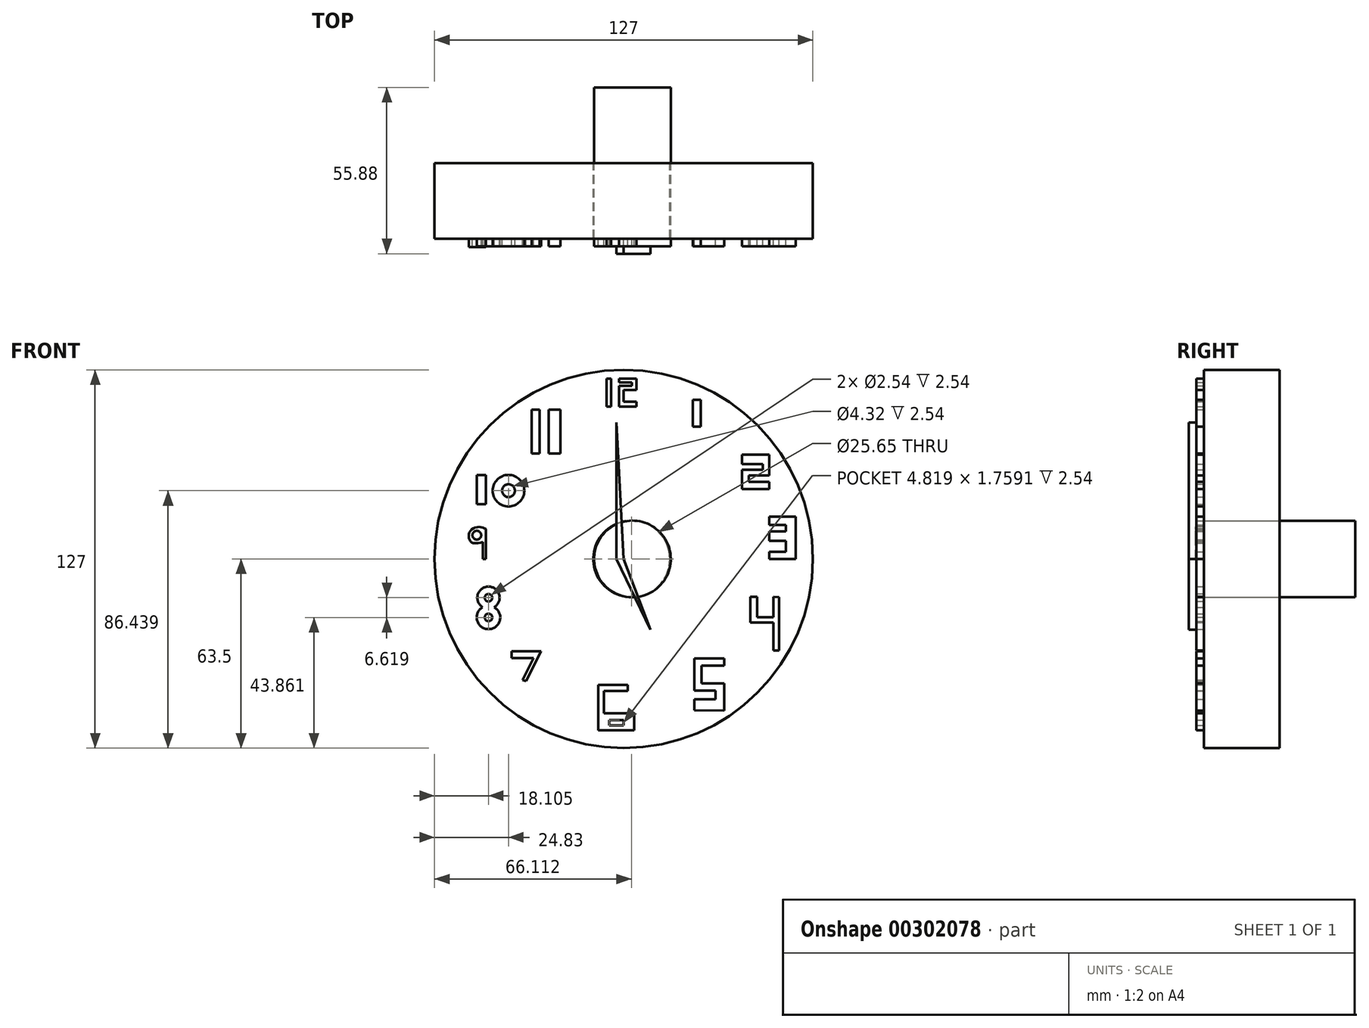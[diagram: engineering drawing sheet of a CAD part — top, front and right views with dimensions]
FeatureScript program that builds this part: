
annotation { "Feature Type Name" : "Feature", "Feature Type Description" : "" }
export const myFeature = defineFeature(function(context is Context, id is Id, definition is map)
    precondition{}
    {
        {
            var Q0;
            Q0=qCreatedBy(makeId("Front.planeOp"),FACE);
            var sketch = newSketch(context, id + "F0", { "sketchPlane" : qUnion([Q0])});
            skCircle(sketch, "E0", {"center": v(0, 0) * mm, "radius": 63.5 * mm});
            skSolve(sketch);
        }
        {
            var Q0;
            Q0 = qSketchRegion(id + "F0", true);
            extrude(context, id + "F1", {"entities" : qUnion([Q0]), "depth" : 25.4 * mm});
        }
        {
            var Q0;
            Q0=makeQuery(id+"F1.opExtrude","CAP_FACE",FACE,{"disambiguationData":[OSD([sQuery(id+"F0.wireOp",EDGE,"E0")])],"isStart":false});
            var sketch = newSketch(context, id + "F2", { "sketchPlane" : qUnion([Q0])});
            skLineSegment(sketch, "E1", {"start": v(-5.79, 60.54) * mm, "end": v(-4.25, 60.54) * mm});
            skLineSegment(sketch, "E2", {"start": v(0, 60.54) * mm, "end": v(4.26, 60.54) * mm});
            skLineSegment(sketch, "E3", {"start": v(4.26, 60.54) * mm, "end": v(4.26, 56.77) * mm});
            skLineSegment(sketch, "E4", {"start": v(4.26, 56.77) * mm, "end": v(0, 56.77) * mm});
            skLineSegment(sketch, "E5", {"start": v(0, 56.77) * mm, "end": v(0, 52.86) * mm});
            skLineSegment(sketch, "E6", {"start": v(0, 52.86) * mm, "end": v(4.26, 52.86) * mm});
            skLineSegment(sketch, "E7", {"start": v(4.26, 52.86) * mm, "end": v(4.26, 51.19) * mm});
            skLineSegment(sketch, "E8", {"start": v(4.26, 51.19) * mm, "end": v(0, 51.19) * mm});
            skLineSegment(sketch, "E9", {"start": v(0, 51.19) * mm, "end": v(-1.6, 51.19) * mm});
            skLineSegment(sketch, "E10", {"start": v(-1.6, 51.19) * mm, "end": v(-1.6, 58.17) * mm});
            skLineSegment(sketch, "E11", {"start": v(-1.6, 58.17) * mm, "end": v(2.73, 58.17) * mm});
            skLineSegment(sketch, "E12", {"start": v(2.73, 58.17) * mm, "end": v(2.73, 59.28) * mm});
            skLineSegment(sketch, "E13", {"start": v(2.73, 59.28) * mm, "end": v(-1.6, 59.28) * mm});
            skLineSegment(sketch, "E14", {"start": v(-1.6, 59.28) * mm, "end": v(-1.6, 60.54) * mm});
            skLineSegment(sketch, "E15", {"start": v(-1.6, 60.54) * mm, "end": v(0, 60.54) * mm});
            skLineSegment(sketch, "E16", {"start": v(-5.79, 60.54) * mm, "end": v(-5.79, 51.19) * mm});
            skLineSegment(sketch, "E17", {"start": v(-5.79, 51.19) * mm, "end": v(-4.25, 51.19) * mm});
            skLineSegment(sketch, "E18", {"start": v(-4.25, 51.19) * mm, "end": v(-4.25, 60.54) * mm});
            skLineSegment(sketch, "E19", {"start": v(23.23, 53.4) * mm, "end": v(23.23, 44.44) * mm});
            skLineSegment(sketch, "E20", {"start": v(23.23, 44.44) * mm, "end": v(25.84, 44.44) * mm});
            skLineSegment(sketch, "E21", {"start": v(25.84, 44.44) * mm, "end": v(25.84, 53.52) * mm});
            skLineSegment(sketch, "E22", {"start": v(25.84, 53.52) * mm, "end": v(23.23, 53.4) * mm});
            skLineSegment(sketch, "E23", {"start": v(39.65, 34.98) * mm, "end": v(48.85, 34.98) * mm});
            skLineSegment(sketch, "E24", {"start": v(39.65, 34.98) * mm, "end": v(39.65, 31.87) * mm});
            skLineSegment(sketch, "E25", {"start": v(39.65, 31.87) * mm, "end": v(46.74, 31.87) * mm});
            skLineSegment(sketch, "E26", {"start": v(46.74, 31.87) * mm, "end": v(46.74, 30) * mm});
            skLineSegment(sketch, "E27", {"start": v(46.74, 30) * mm, "end": v(39.65, 30) * mm});
            skLineSegment(sketch, "E28", {"start": v(39.65, 30) * mm, "end": v(39.65, 23.54) * mm});
            skLineSegment(sketch, "E29", {"start": v(39.65, 23.54) * mm, "end": v(48.85, 23.54) * mm});
            skLineSegment(sketch, "E30", {"start": v(48.85, 23.54) * mm, "end": v(48.85, 25.9) * mm});
            skLineSegment(sketch, "E31", {"start": v(48.85, 25.9) * mm, "end": v(42.01, 25.9) * mm});
            skLineSegment(sketch, "E32", {"start": v(42.01, 25.9) * mm, "end": v(42.01, 28.02) * mm});
            skLineSegment(sketch, "E33", {"start": v(42.01, 28.02) * mm, "end": v(48.85, 28.02) * mm});
            skLineSegment(sketch, "E34", {"start": v(48.85, 28.02) * mm, "end": v(48.85, 34.98) * mm});
            skLineSegment(sketch, "E35", {"start": v(48.85, 14.26) * mm, "end": v(48.85, 11.36) * mm});
            skLineSegment(sketch, "E36", {"start": v(48.85, 14.26) * mm, "end": v(57.8, 14.26) * mm});
            skLineSegment(sketch, "E37", {"start": v(57.8, 14.26) * mm, "end": v(57.8, 11.36) * mm});
            skLineSegment(sketch, "E38", {"start": v(57.8, 11.36) * mm, "end": v(57.8, 0) * mm});
            skLineSegment(sketch, "E39", {"start": v(48.85, 11.36) * mm, "end": v(54.45, 11.36) * mm});
            skLineSegment(sketch, "E40", {"start": v(54.45, 11.36) * mm, "end": v(54.45, 9.25) * mm});
            skLineSegment(sketch, "E41", {"start": v(54.45, 9.25) * mm, "end": v(48.85, 9.25) * mm});
            skLineSegment(sketch, "E42", {"start": v(48.85, 9.25) * mm, "end": v(48.85, 6.08) * mm});
            skLineSegment(sketch, "E43", {"start": v(48.85, 6.08) * mm, "end": v(54.45, 6.08) * mm});
            skLineSegment(sketch, "E44", {"start": v(54.45, 6.08) * mm, "end": v(54.45, 2.39) * mm});
            skLineSegment(sketch, "E45", {"start": v(54.45, 2.39) * mm, "end": v(48.85, 2.39) * mm});
            skLineSegment(sketch, "E46", {"start": v(48.85, 2.39) * mm, "end": v(48.85, 0) * mm});
            skLineSegment(sketch, "E47", {"start": v(48.85, 0) * mm, "end": v(57.8, 0) * mm});
            skLineSegment(sketch, "E48", {"start": v(42.48, -12.73) * mm, "end": v(42.48, -21.35) * mm});
            skLineSegment(sketch, "E49", {"start": v(42.48, -21.35) * mm, "end": v(50.24, -21.35) * mm});
            skLineSegment(sketch, "E50", {"start": v(52.2, -21.35) * mm, "end": v(52.2, -12.81) * mm});
            skLineSegment(sketch, "E51", {"start": v(52.2, -21.35) * mm, "end": v(52.2, -30.75) * mm});
            skLineSegment(sketch, "E52", {"start": v(52.2, -30.75) * mm, "end": v(50.24, -30.75) * mm});
            skLineSegment(sketch, "E53", {"start": v(50.24, -30.75) * mm, "end": v(50.24, -21.35) * mm});
            skLineSegment(sketch, "E54", {"start": v(42.48, -12.73) * mm, "end": v(44.75, -12.73) * mm});
            skLineSegment(sketch, "E55", {"start": v(44.75, -12.73) * mm, "end": v(44.75, -19.63) * mm});
            skLineSegment(sketch, "E56", {"start": v(44.75, -19.63) * mm, "end": v(50.24, -19.63) * mm});
            skLineSegment(sketch, "E57", {"start": v(50.24, -19.63) * mm, "end": v(50.24, -12.73) * mm});
            skLineSegment(sketch, "E58", {"start": v(50.24, -12.73) * mm, "end": v(52.2, -12.81) * mm});
            skLineSegment(sketch, "E59", {"start": v(33.76, -33.37) * mm, "end": v(33.76, -35.85) * mm});
            skLineSegment(sketch, "E60", {"start": v(33.76, -35.85) * mm, "end": v(26.17, -35.85) * mm});
            skLineSegment(sketch, "E61", {"start": v(26.17, -35.85) * mm, "end": v(26.17, -41.83) * mm});
            skLineSegment(sketch, "E62", {"start": v(26.17, -41.83) * mm, "end": v(33.76, -41.83) * mm});
            skLineSegment(sketch, "E63", {"start": v(33.76, -41.83) * mm, "end": v(33.76, -50.9) * mm});
            skLineSegment(sketch, "E64", {"start": v(33.76, -33.37) * mm, "end": v(23.77, -33.37) * mm});
            skLineSegment(sketch, "E65", {"start": v(23.77, -33.37) * mm, "end": v(23.77, -44.2) * mm});
            skLineSegment(sketch, "E66", {"start": v(23.77, -44.2) * mm, "end": v(30.78, -44.2) * mm});
            skLineSegment(sketch, "E67", {"start": v(30.78, -44.2) * mm, "end": v(30.78, -47.15) * mm});
            skLineSegment(sketch, "E68", {"start": v(30.78, -47.15) * mm, "end": v(23.77, -47.15) * mm});
            skLineSegment(sketch, "E69", {"start": v(23.77, -47.15) * mm, "end": v(23.77, -50.8) * mm});
            skLineSegment(sketch, "E70", {"start": v(23.77, -50.8) * mm, "end": v(33.76, -50.9) * mm});
            skLineSegment(sketch, "E71", {"start": v(-8.51, -42.29) * mm, "end": v(-8.51, -57.6) * mm});
            skLineSegment(sketch, "E72", {"start": v(-8.51, -57.6) * mm, "end": v(3.54, -57.6) * mm});
            skLineSegment(sketch, "E73", {"start": v(3.54, -57.6) * mm, "end": v(3.54, -51.88) * mm});
            skLineSegment(sketch, "E74", {"start": v(3.54, -51.88) * mm, "end": v(-6.67, -51.88) * mm});
            skLineSegment(sketch, "E75", {"start": v(-8.51, -42.29) * mm, "end": v(1.34, -42.29) * mm});
            skLineSegment(sketch, "E76", {"start": v(1.34, -42.29) * mm, "end": v(1.34, -44.31) * mm});
            skLineSegment(sketch, "E77", {"start": v(1.34, -44.31) * mm, "end": v(-6.67, -44.31) * mm});
            skLineSegment(sketch, "E78", {"start": v(-6.67, -44.31) * mm, "end": v(-6.67, -51.88) * mm});
            skPoint(sketch, "E79.orphan", {"position": v(-8.51, -51.88) * mm});
            skLineSegment(sketch, "E80", {"start": v(-4.82, -54.16) * mm, "end": v(-4.82, -55.83) * mm});
            skLineSegment(sketch, "E81", {"start": v(-4.82, -55.83) * mm, "end": v(0, -55.83) * mm});
            skLineSegment(sketch, "E82", {"start": v(-4.82, -54.16) * mm, "end": v(0, -54.07) * mm});
            skLineSegment(sketch, "E83", {"start": v(0, -54.07) * mm, "end": v(0, -55.83) * mm});
            skSolve(sketch);
        }
        {
            var Q0;
            Q0=makeQuery(id+"F2.imprint","IMPRINT",FACE,{"disambiguationData":[TD([[makeQuery(id+"F2.imprint","IMPRINT",EDGE,{"derivedFrom":makeQuery(id+"F1.opExtrude","CAP_EDGE",EDGE,{"disambiguationData":[OSD([sQuery(id+"F0.wireOp",EDGE,"E0")])],"isStart":false})}),1.0]])]});
            var sketch = newSketch(context, id + "F3", { "sketchPlane" : qUnion([Q0])});
            skLineSegment(sketch, "E84", {"start": v(-32.8, -41.1) * mm, "end": v(-27.77, -31.01) * mm});
            skLineSegment(sketch, "E85", {"start": v(-27.77, -31.01) * mm, "end": v(-37.61, -31.01) * mm});
            skLineSegment(sketch, "E86", {"start": v(-37.61, -31.01) * mm, "end": v(-37.61, -33.3) * mm});
            skLineSegment(sketch, "E87", {"start": v(-37.61, -33.3) * mm, "end": v(-30.29, -33.3) * mm});
            skPoint(sketch, "E87.endSnap0", {"position": v(-30.29, -36.05) * mm});
            skLineSegment(sketch, "E88", {"start": v(-30.29, -33.3) * mm, "end": v(-33.95, -40.63) * mm});
            skLineSegment(sketch, "E89", {"start": v(-33.95, -40.63) * mm, "end": v(-32.8, -41.1) * mm});
            skArc(sketch, "E90", {"start": v(-47.35, -16.21) * mm, "mid": v(-45.4, -23.58) * mm, "end": v(-43.44, -16.21) * mm});
            skArc(sketch, "E91", {"start": v(-43.44, -16.21) * mm, "mid": v(-45.4, -9.28) * mm, "end": v(-47.35, -16.21) * mm});
            skLineSegment(sketch, "E92", {"start": v(-49.28, 18.45) * mm, "end": v(-49.28, 28.24) * mm});
            skLineSegment(sketch, "E93", {"start": v(-49.28, 28.24) * mm, "end": v(-46.29, 28.24) * mm});
            skLineSegment(sketch, "E94", {"start": v(-46.29, 28.24) * mm, "end": v(-46.29, 18.45) * mm});
            skLineSegment(sketch, "E95", {"start": v(-46.29, 18.45) * mm, "end": v(-49.28, 18.45) * mm});
            skCircle(sketch, "E96", {"center": v(-38.67, 22.94) * mm, "radius": 5.3 * mm});
            skLineSegment(sketch, "E97", {"start": v(-30.92, 50.15) * mm, "end": v(-30.92, 35.45) * mm});
            skLineSegment(sketch, "E98", {"start": v(-30.92, 35.45) * mm, "end": v(-28.2, 35.45) * mm});
            skLineSegment(sketch, "E99", {"start": v(-28.2, 35.45) * mm, "end": v(-28.2, 50.15) * mm});
            skLineSegment(sketch, "E100", {"start": v(-28.2, 50.15) * mm, "end": v(-30.92, 50.15) * mm});
            skLineSegment(sketch, "E101", {"start": v(-25.14, 50.15) * mm, "end": v(-25.14, 35.45) * mm});
            skLineSegment(sketch, "E102", {"start": v(-25.14, 35.45) * mm, "end": v(-21.29, 35.45) * mm});
            skLineSegment(sketch, "E103", {"start": v(-21.29, 35.45) * mm, "end": v(-21.29, 50.15) * mm});
            skLineSegment(sketch, "E104", {"start": v(-21.29, 50.15) * mm, "end": v(-25.14, 50.15) * mm});
            skCircle(sketch, "E105", {"center": v(-45.4, -13.02) * mm, "radius": 1.27 * mm});
            skCircle(sketch, "E106", {"center": v(-45.4, -19.64) * mm, "radius": 1.27 * mm});
            skCircle(sketch, "E107", {"center": v(-38.67, 22.94) * mm, "radius": 2.16 * mm});
            skSolve(sketch);
        }
        {
            var Q0;
            Q0=makeQuery(id+"F2.imprint","IMPRINT",FACE,{"disambiguationData":[TD([[makeQuery(id+"F2.imprint","IMPRINT",EDGE,{"derivedFrom":sQuery(id+"F2.wireOp",EDGE,"E1")}),1.0]])]});
            var sketch = newSketch(context, id + "F4", { "sketchPlane" : qUnion([Q0])});
            skLineSegment(sketch, "E108", {"start": v(-46.28, 10.07) * mm, "end": v(-46.28, 0) * mm});
            skLineSegment(sketch, "E109", {"start": v(-46.28, 0) * mm, "end": v(-47.31, 0) * mm});
            skLineSegment(sketch, "E110", {"start": v(-47.31, 0) * mm, "end": v(-47.31, 5.65) * mm});
            skFitSpline(sketch, "E111", {"points": [v(-47.31, 5.65) * mm, v(-51.19, 5.65) * mm, v(-51.8, 8.8) * mm, v(-48.36, 10.76) * mm, v(-46.28, 10.07) * mm, v(-46.28, 10.07) * mm], "startDerivative": vector(-18, -4.06) * mm, "endDerivative": vector(287.85, 154.16) * mm});
            skCircle(sketch, "E112", {"center": v(-49.3, 7.98) * mm, "radius": 1.48 * mm});
            skSolve(sketch);
        }
        {
            var Q0;
            Q0=makeQuery(id+"F3.imprint","IMPRINT",FACE,{"disambiguationData":[TD([[makeQuery(id+"F3.imprint","IMPRINT",EDGE,{"derivedFrom":sQuery(id+"F3.wireOp",EDGE,"E84")}),1.0]])]});
            var Q1;
            Q1=makeQuery(id+"F3.imprint","IMPRINT",FACE,{"disambiguationData":[TD([[makeQuery(id+"F3.imprint","IMPRINT",EDGE,{"derivedFrom":sQuery(id+"F3.wireOp",EDGE,"E90")}),1.0]])]});
            var Q2;
            Q2=makeQuery(id+"F3.imprint","IMPRINT",FACE,{"disambiguationData":[TD([[makeQuery(id+"F3.imprint","IMPRINT",EDGE,{"derivedFrom":sQuery(id+"F3.wireOp",EDGE,"E96")}),1.0]])]});
            var Q3;
            Q3=makeQuery(id+"F3.imprint","IMPRINT",FACE,{"disambiguationData":[TD([[makeQuery(id+"F3.imprint","IMPRINT",EDGE,{"derivedFrom":sQuery(id+"F3.wireOp",EDGE,"E92")}),-1.0]])]});
            var Q4;
            Q4=makeQuery(id+"F3.imprint","IMPRINT",FACE,{"disambiguationData":[TD([[makeQuery(id+"F3.imprint","IMPRINT",EDGE,{"derivedFrom":sQuery(id+"F3.wireOp",EDGE,"E97")}),1.0]])]});
            var Q5;
            Q5=makeQuery(id+"F3.imprint","IMPRINT",FACE,{"disambiguationData":[TD([[makeQuery(id+"F3.imprint","IMPRINT",EDGE,{"derivedFrom":sQuery(id+"F3.wireOp",EDGE,"E101")}),1.0]])]});
            extrude(context, id + "F5", {"entities" : qUnion([Q0, Q1, Q2, Q3, Q4, Q5]), "operationType" : NewBodyOperationType.ADD, "depth" : 2.54 * mm});
        }
        {
            var Q0;
            Q0 = qSketchRegion(id + "F2", true);
            var Q1;
            Q1=makeQuery(id+"F4.imprint","IMPRINT",FACE,{"disambiguationData":[TD([[makeQuery(id+"F4.imprint","IMPRINT",EDGE,{"derivedFrom":makeQuery(id+"F2.imprint","IMPRINT",EDGE,{"derivedFrom":sQuery(id+"F2.wireOp",EDGE,"E48")})}),1.0]])]});
            extrude(context, id + "F6", {"entities" : qUnion([Q0, Q1]), "operationType" : NewBodyOperationType.ADD, "depth" : 2.54 * mm});
        }
        {
            var Q0;
            {var subQ1=sQuery(id+"F4.wireOp",EDGE,"E109");Q0=makeQuery(id+"F4.imprint","IMPRINT",FACE,{"disambiguationData":[TD([[makeQuery(id+"F4.imprint","IMPRINT",EDGE,{"derivedFrom":subQ1}),-1.0]])]});}
            extrude(context, id + "F7", {"entities" : qUnion([Q0]), "operationType" : NewBodyOperationType.ADD, "depth" : 2.54 * mm});
        }
        {
            var Q0;
            Q0 = qSketchRegion(id + "F2", true);
            extrude(context, id + "F8", {"entities" : qUnion([Q0]), "operationType" : NewBodyOperationType.ADD, "depth" : 2.54 * mm});
        }
        {
            var Q0;
            Q0=makeQuery(id+"F1.opExtrude","CAP_FACE",FACE,{"disambiguationData":[OSD([sQuery(id+"F0.wireOp",EDGE,"E0")])],"isStart":true});
            cPlane(context, id + "F9", {"entities" : qUnion([Q0]), "cplaneType" : CPlaneType.OFFSET, "offset" : 25.4 * mm, "width" : 152.4 * mm, "height" : 152.4 * mm});
        }
        {
            var Q0;
            Q0=qCreatedBy(makeId("Front.planeOp"),FACE);
            cPlane(context, id + "F10", {"entities" : qUnion([Q0]), "cplaneType" : CPlaneType.OFFSET, "offset" : 27.94 * mm, "width" : 152.4 * mm, "height" : 152.4 * mm});
        }
        {
            var Q0;
            Q0=makeQuery(id+"F1.opExtrude","CAP_FACE",FACE,{"disambiguationData":[OSD([sQuery(id+"F0.wireOp",EDGE,"E0")])],"isStart":true});
            var sketch = newSketch(context, id + "F11", { "sketchPlane" : qUnion([Q0])});
            skPoint(sketch, "E113", {"position": v(0, 0) * mm});
            skPoint(sketch, "E114", {"position": v(0, 0.21) * mm});
            skCircle(sketch, "E115", {"center": v(-2.61, 0) * mm, "radius": 5.53 * mm});
            skSolve(sketch);
        }
        {
            var Q0;
            Q0=sQuery(id+"F11.wireOp",VERTEX,"E115.center");
            var Q1;
            Q1=makeQuery(id+"F1.opExtrude","SWEPT_BODY",BODY,{"disambiguationData":[OSD([sQuery(id+"F0.wireOp",EDGE,"E0")])]});
            hole(context, id + "F12", {"style" : HoleStyle.SIMPLE, "endStyle" : HoleEndStyle.THROUGH, "holeDiameter" : 25.65 * mm, "tappedDepth" : 12.7 * mm, "tapClearance" : 3, "locations" : qUnion([Q0]), "scope" : qUnion([Q1])});
        }
        {
            var Q0;
            Q0=qCreatedBy(id+"F10.planeOp",FACE);
            var sketch = newSketch(context, id + "F13", { "sketchPlane" : qUnion([Q0])});
            skLineSegment(sketch, "E116", {"start": v(0, 0) * mm, "end": v(-2.47, 0) * mm});
            skLineSegment(sketch, "E117", {"start": v(-2.47, 0) * mm, "end": v(-2.47, 45.83) * mm});
            skLineSegment(sketch, "E118", {"start": v(-2.47, 45.83) * mm, "end": v(0, 0) * mm});
            skLineSegment(sketch, "E119", {"start": v(-2.47, 0) * mm, "end": v(8.94, -23.74) * mm});
            skLineSegment(sketch, "E120", {"start": v(0, 0) * mm, "end": v(8.94, -23.74) * mm});
            skSolve(sketch);
        }
        {
            var Q0;
            Q0 = qSketchRegion(id + "F13", true);
            extrude(context, id + "F14", {"entities" : qUnion([Q0]), "operationType" : NewBodyOperationType.ADD, "depth" : 2.54 * mm});
        }
        {
            var Q0;
            Q0=makeQuery(id+"F7.opExtrude","CAP_FACE",FACE,{"disambiguationData":[OSD([sQuery(id+"F4.wireOp",EDGE,"E108"),sQuery(id+"F4.wireOp",EDGE,"E109"),sQuery(id+"F4.wireOp",EDGE,"E110"),sQuery(id+"F4.wireOp",EDGE,"E111"),sQuery(id+"F4.wireOp",EDGE,"E112")])],"isStart":false});
            extrude(context, id + "F15", {"entities" : qUnion([Q0]), "operationType" : NewBodyOperationType.ADD, "depth" : 0.25 * mm});
        }
        {
            var Q0;
            Q0=qCreatedBy(makeId("Front.planeOp"),FACE);
            var sketch = newSketch(context, id + "F16", { "sketchPlane" : qUnion([Q0])});
            skCircle(sketch, "E121", {"center": v(2.92, 0) * mm, "radius": 12.88 * mm});
            skSolve(sketch);
        }
        {
            var Q0;
            Q0 = qSketchRegion(id + "F16", true);
            extrude(context, id + "F17", {"entities" : qUnion([Q0]), "depth" : 27.94 * mm});
        }
        {
            var Q0;
            Q0 = qSketchRegion(id + "F16", true);
            extrude(context, id + "F18", {"entities" : qUnion([Q0]), "oppositeDirection" : true, "depth" : 25.4 * mm});
        }
    });
